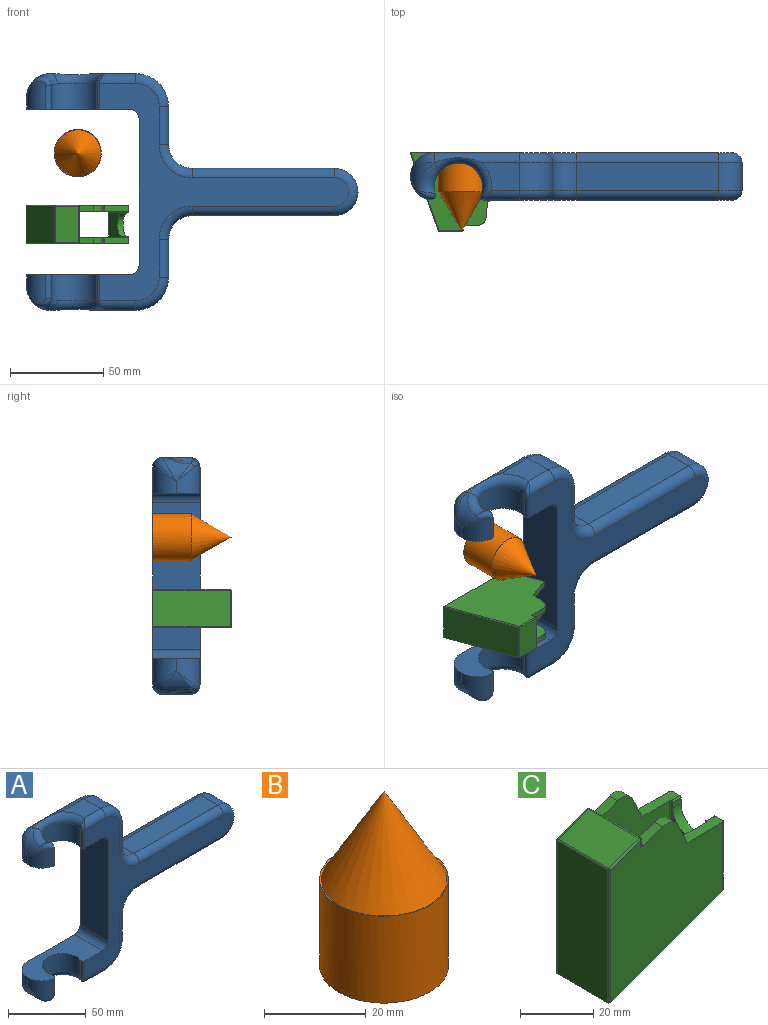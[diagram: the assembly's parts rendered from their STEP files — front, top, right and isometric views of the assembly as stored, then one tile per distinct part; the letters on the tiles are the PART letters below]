
ASSEMBLY  parts=3 mates=2
PART A: 69 faces, bbox 178.8x31.9x135.7 mm
  f0: plane 0.95x0.92mm, normal (0,0,-1), area 0.4mm2, adj f1,f67,f68
  f1: cylinder r=12.7mm len=15.32mm, axis (0,-1,0), area 116.5mm2, adj f0,f2,f64,f65,f66
  f2: bspline ~15x12.7mm, area 107.5mm2, adj f1,f3,f68
  f3: cylinder r=12.7mm len=13.97mm, axis (0,0,-1), area 202.7mm2, adj f2,f4,f63,f64
  f4: plane 55.25x25.4mm, normal (0,0,1), area 896.5mm2, adj f3,f5,f57,f58,f59,f60,f62,f63
  f5: cylinder r=5.08mm len=25.4mm, axis (0,-1,0), area 202.7mm2, adj f4,f6,f57,f63
  f6: plane 78.74x25.4mm, normal (-1,0,0), area 2000mm2, adj f5,f7,f57,f63
  f7: cylinder r=5.08mm len=25.4mm, axis (0,1,0), area 202.7mm2, adj f6,f8,f57,f63
  f8: plane 55.25x25.4mm, normal (0,0,-1), area 896.5mm2, adj f7,f9,f52,f53,f54,f55,f56,f57
  f9: cylinder r=1.59mm len=13.97mm, axis (0,0,1), area 43.1mm2, adj f8,f10,f56,f57
  f10: bspline ~6.71x6.3mm, area 11.8mm2, adj f9,f11,f51
  f11: torus R=18.03mm, axis (0,0,-1), area 267.3mm2, adj f10,f12,f43,f49,f50,f56
  f12: plane 20.77x15.24mm, normal (0,0,1), area 249.5mm2, adj f11,f13,f50,f51
  f13: cylinder r=17.78mm len=17.78mm, axis (0,1,0), area 425.6mm2, adj f12,f14,f41,f42
  f14: torus R=12.7mm, axis (0,-1,0), area 199.7mm2, adj f13,f15,f51,f57
  f15: cylinder r=5.08mm len=20.32mm, axis (0,0,1), area 162.1mm2, adj f14,f16,f42,f57
  f16: torus R=17.78mm, axis (0,-1,0), area 182.3mm2, adj f15,f17,f40,f57
  f17: cylinder r=12.7mm len=15.24mm, axis (0,1,0), area 304mm2, adj f16,f18,f38,f42
  f18: plane 76.2x15.24mm, normal (0,0,1), area 1161.3mm2, adj f17,f19,f37,f40
  f19: cylinder r=5.08mm len=76.2mm, axis (1,0,0), area 608mm2, adj f18,f20,f38,f63
  f20: torus R=7.62mm, axis (0,-1,0), area 272.1mm2, adj f19,f21,f37,f63
  f21: cylinder r=5.08mm len=76.2mm, axis (-1,0,0), area 608mm2, adj f20,f22,f36,f63
  f22: plane 76.2x15.24mm, normal (0,0,-1), area 1161.3mm2, adj f21,f23,f35,f37
  f23: cylinder r=5.08mm len=76.2mm, axis (1,0,0), area 608mm2, adj f22,f24,f25,f57
  f24: torus R=7.62mm, axis (0,-1,0), area 272.1mm2, adj f23,f37,f40,f57
  f25: torus R=17.78mm, axis (0,-1,0), area 182.3mm2, adj f23,f26,f35,f57
  f26: cylinder r=5.08mm len=20.32mm, axis (0,0,1), area 162.1mm2, adj f25,f27,f34,f57
  f27: plane 20.32x15.24mm, normal (1,0,0), area 309.7mm2, adj f26,f28,f30,f35
  f28: cylinder r=5.08mm len=20.32mm, axis (0,0,-1), area 162.1mm2, adj f27,f29,f36,f63
  f29: torus R=12.7mm, axis (0,-1,0), area 199.7mm2, adj f28,f30,f63,f68
  f30: cylinder r=17.78mm len=17.78mm, axis (0,1,0), area 425.6mm2, adj f27,f29,f31,f34
  f31: plane 20.77x15.24mm, normal (0,0,-1), area 249.5mm2, adj f30,f32,f67,f68
  f32: cylinder r=5.08mm len=19.21mm, axis (-1,0,0), area 135.8mm2, adj f31,f33,f34,f57
  f33: bspline ~6.71x6.3mm, area 11.7mm2, adj f32,f58,f67
  f34: torus R=12.7mm, axis (0,-1,0), area 199.7mm2, adj f26,f30,f32,f57
  f35: cylinder r=12.7mm len=15.24mm, axis (0,1,0), area 304mm2, adj f22,f25,f27,f36
  f36: torus R=17.78mm, axis (0,-1,0), area 182.3mm2, adj f21,f28,f35,f63
  f37: cylinder r=12.7mm len=25.4mm, axis (0,-1,0), area 608mm2, adj f18,f20,f22,f24
  f38: torus R=17.78mm, axis (0,-1,0), area 182.3mm2, adj f17,f19,f39,f63
  f39: cylinder r=5.08mm len=20.32mm, axis (0,0,-1), area 162.1mm2, adj f38,f41,f42,f63
  f40: cylinder r=5.08mm len=76.2mm, axis (-1,0,0), area 608mm2, adj f16,f18,f24,f57
  f41: torus R=12.7mm, axis (0,-1,0), area 199.7mm2, adj f13,f39,f50,f63
  f42: plane 20.32x15.24mm, normal (1,0,0), area 309.7mm2, adj f13,f15,f17,f39
  f43: bspline ~20.18x13.12mm, area 151.9mm2, adj f11,f44,f46,f56
  f44: bspline ~11.04x6.91mm, area 51.1mm2, adj f43,f45,f54,f55
  f45: bspline ~10.21x10.21mm, area 13.2mm2, adj f44,f46,f54
  f46: cylinder r=12.7mm len=15.32mm, axis (0,1,0), area 116.5mm2, adj f43,f45,f47,f48,f49,f53
  f47: bspline ~13.31x8.06mm, area 42.8mm2, adj f46,f50,f52
  f48: bspline ~9.27x9.27mm, area 10.4mm2, adj f46,f52
  f49: plane 0.95x0.92mm, normal (0,0,1), area 0.4mm2, adj f11,f46,f50
  f50: cylinder r=5.08mm len=45.72mm, axis (-1,0,0), area 327.3mm2, adj f11,f12,f41,f47,f49,f63
  f51: cylinder r=5.08mm len=19.21mm, axis (1,0,0), area 135.8mm2, adj f10,f12,f14,f57
  f52: cylinder r=12.7mm len=13.97mm, axis (0,0,-1), area 202.7mm2, adj f8,f47,f48,f53,f63
  f53: plane 6.35x0.01mm, normal (-1,0,0), area 0.1mm2, adj f8,f46,f52,f54
  f54: cylinder r=12.7mm len=14.04mm, axis (0,0,-1), area 198.4mm2, adj f8,f44,f45,f53,f55
  f55: cylinder r=2.54mm len=12.55mm, axis (0,0,1), area 65mm2, adj f8,f44,f54,f56
  f56: cylinder r=12.95mm len=25.91mm, axis (0,0,1), area 675mm2, adj f8,f9,f11,f43,f55
  f57: plane 133.51x116.84mm, normal (0,-1,0), area 3452.3mm2, adj f4,f5,f6,f7,f8,f9,f14,f15
  f58: cylinder r=1.59mm len=13.97mm, axis (0,0,1), area 43.1mm2, adj f4,f33,f57,f59
  f59: cylinder r=12.95mm len=25.91mm, axis (0,0,1), area 675mm2, adj f4,f58,f60,f66,f67
  f60: cylinder r=2.54mm len=12.55mm, axis (0,0,-1), area 65mm2, adj f4,f59,f61,f62
  f61: bspline ~11.04x6.91mm, area 51.1mm2, adj f60,f62,f65,f66
  f62: cylinder r=12.7mm len=14.04mm, axis (0,0,-1), area 198.4mm2, adj f4,f60,f61,f64,f65
  f63: plane 160.02x116.84mm, normal (0,1,0), area 4192.9mm2, adj f3,f4,f5,f6,f7,f8,f19,f20
  f64: plane 6.35x0.01mm, normal (-1,0,0), area 0.1mm2, adj f1,f3,f4,f62
  f65: bspline ~10.21x10.21mm, area 13.2mm2, adj f1,f61,f62
  f66: bspline ~19.02x13.12mm, area 151.9mm2, adj f1,f59,f61,f67
  f67: torus R=18.03mm, axis (0,0,-1), area 267.3mm2, adj f0,f31,f33,f59,f66,f68
  f68: cylinder r=5.08mm len=45.72mm, axis (1,0,0), area 327.3mm2, adj f0,f2,f29,f31,f63,f67
PART B: 4 faces, bbox 25.4x25.4x42.2 mm
  f0: plane 25.4x25.4mm, normal (0,0,-1), area 506.7mm2, adj f1
  f1: cylinder r=12.7mm len=25.4mm, axis (0,0,1), area 1672.1mm2, adj f0,f2
  f2: cone r=12.7mm half-angle=60deg, axis (0,0,1), area 30mm2, adj f1,f3
  f3: cone r=12.37mm half-angle=30deg, axis (0,0,-1), area 961.4mm2, adj f2
PART C: 63 faces, bbox 44.7x21.9x49.5 mm
  f0: plane 6.35x6.35mm, normal (0.34,0,-0.94), area 42.9mm2, adj f1,f7,f8,f9
  f1: plane 10.72x6.35mm, normal (1,0,0), area 68.1mm2, adj f0,f7,f9,f10
  f2: sphere r=0.5mm, area 0.3mm2, adj f6,f12,f13
  f3: sphere r=0.5mm, area 0.3mm2, adj f6,f19,f20
  f4: plane 19.64x11.7mm, normal (-0.34,0,0.94), area 244.5mm2, adj f6,f13,f19,f28
  f5: cylinder r=0.5mm len=2.68mm, axis (0,-1,0), area 2.6mm2, adj f21,f22,f31,f40
  f6: cylinder r=0.5mm len=19.64mm, axis (0,-1,0), area 18.9mm2, adj f2,f3,f4,f40
  f7: plane 14.51x7.39mm, normal (0,1,0), area 75.3mm2, adj f0,f1,f8,f10,f42
  f8: plane 11.83x6.35mm, normal (-1,0,0), area 75.1mm2, adj f0,f7,f9,f42
  f9: plane 14.51x7.39mm, normal (0,-1,0), area 75.3mm2, adj f0,f1,f8,f10,f42
  f10: cylinder r=1.57mm len=6.35mm, axis (0,1,0), area 12.2mm2, adj f1,f7,f9,f42
  f11: bspline ~1.19x1.01mm, area 0.6mm2, adj f12,f38,f39,f44
  f12: cylinder r=0.5mm len=2.31mm, axis (0,0,-1), area 1.7mm2, adj f2,f11,f40,f44
  f13: cylinder r=0.5mm len=11.87mm, axis (0.94,0,0.34), area 9.8mm2, adj f2,f4,f29,f44
  f14: cylinder r=0.5mm len=3.22mm, axis (1,0,0), area 2.5mm2, adj f15,f26,f32,f33,f46
  f15: plane 3.18x1.88mm, normal (0,-1,0), area 6mm2, adj f14,f16,f33,f46
  f16: cylinder r=6.35mm len=12.7mm, axis (-1,0,0), area 63.3mm2, adj f15,f17,f33,f46
  f17: plane 3.18x1.88mm, normal (0,1,0), area 6mm2, adj f16,f18,f33,f46
  f18: cylinder r=0.5mm len=3.22mm, axis (-1,0,0), area 2.5mm2, adj f17,f33,f34,f41,f46
  f19: cylinder r=0.5mm len=11.87mm, axis (-0.94,0,-0.34), area 9.8mm2, adj f3,f4,f27,f48
  f20: cylinder r=0.5mm len=2.31mm, axis (0,0,1), area 1.7mm2, adj f3,f21,f40,f48
  f21: bspline ~1.19x1.01mm, area 0.6mm2, adj f5,f20,f22,f48
  f22: plane 7.42x3.19mm, normal (-0.34,0,0.94), area 24.6mm2, adj f5,f21,f23,f31,f48
  f23: cylinder r=4.76mm len=5.94mm, axis (0,1,0), area 22.4mm2, adj f22,f24,f31,f48
  f24: plane 7.32x3.45mm, normal (0.9,0,0.43), area 25.7mm2, adj f23,f25,f31,f48
  f25: cylinder r=0.5mm len=3.18mm, axis (0,1,0), area 1.8mm2, adj f24,f26,f31,f48
  f26: plane 13.97x3.47mm, normal (0,0,1), area 45.3mm2, adj f14,f25,f31,f32,f46,f47,f48
  f27: sphere r=0.5mm, area 0.2mm2, adj f19,f28,f49
  f28: cylinder r=0.5mm len=19.64mm, axis (0,-1,0), area 12mm2, adj f4,f27,f29,f50
  f29: sphere r=0.5mm, area 0.2mm2, adj f13,f28,f51
  f30: cylinder r=0.5mm len=40.86mm, axis (0,0,-1), area 31.8mm2, adj f31,f42,f43,f52
  f31: plane 46.85x37.1mm, normal (0,-1,0), area 1291.2mm2, adj f5,f22,f23,f24,f25,f26,f30,f32
  f32: cylinder r=0.5mm len=22.94mm, axis (0,0,-1), area 17.7mm2, adj f14,f26,f31,f33,f54
  f33: plane 22.35x13.29mm, normal (-1,0,0), area 203.8mm2, adj f14,f15,f16,f17,f18,f32,f41,f55
  f34: plane 13.97x3.47mm, normal (0,0,1), area 45.3mm2, adj f18,f35,f41,f44,f45,f46,f56
  f35: cylinder r=0.5mm len=3.18mm, axis (0,1,0), area 1.8mm2, adj f34,f36,f44,f56
  f36: plane 7.32x3.45mm, normal (0.9,0,0.43), area 25.7mm2, adj f35,f37,f44,f56
  f37: cylinder r=4.76mm len=5.94mm, axis (0,1,0), area 22.4mm2, adj f36,f38,f44,f56
  f38: plane 7.42x3.19mm, normal (-0.34,0,0.94), area 24.6mm2, adj f11,f37,f39,f44,f56
  f39: cylinder r=0.5mm len=2.68mm, axis (0,-1,0), area 2.6mm2, adj f11,f38,f40,f56
  f40: plane 19.64x2.66mm, normal (1,0,0), area 48.5mm2, adj f5,f6,f12,f20,f31,f39,f42,f56
  f41: cylinder r=0.5mm len=22.94mm, axis (0,0,1), area 17.7mm2, adj f18,f33,f34,f56,f57
  f42: plane 14.39x9.62mm, normal (0.34,0,-0.94), area 94.8mm2, adj f7,f8,f9,f10,f30,f31,f40,f43
  f43: plane 40.68x13.29mm, normal (1,0,0), area 540.5mm2, adj f30,f42,f58,f59
  f44: plane 49.3x43.68mm, normal (0,-1,0), area 1569.8mm2, adj f11,f12,f13,f34,f35,f36,f37,f38
  f45: cylinder r=0.5mm len=22.85mm, axis (0,0,1), area 17.9mm2, adj f34,f44,f46,f60
  f46: plane 22.66x19.64mm, normal (1,0,0), area 351.4mm2, adj f14,f15,f16,f17,f18,f26,f34,f45
  f47: cylinder r=0.5mm len=22.85mm, axis (0,0,-1), area 17.9mm2, adj f26,f46,f48,f60
  f48: plane 49.3x43.68mm, normal (0,1,0), area 1569.8mm2, adj f19,f20,f21,f22,f23,f24,f25,f26
  f49: cylinder r=0.5mm len=44.41mm, axis (0,0,-1), area 34.8mm2, adj f27,f48,f50,f60
  f50: plane 44.41x19.64mm, normal (-1,0,0), area 872.1mm2, adj f28,f49,f51,f60
  f51: cylinder r=0.5mm len=44.41mm, axis (0,0,1), area 34.8mm2, adj f29,f44,f50,f60
  f52: bspline ~1.54x1.52mm, area 2.1mm2, adj f30,f53,f59,f60
  f53: cylinder r=1mm len=37.44mm, axis (0.94,0,0.34), area 62mm2, adj f31,f52,f54,f60
  f54: bspline ~1.87x1.54mm, area 2.4mm2, adj f32,f53,f55,f60
  f55: cylinder r=1mm len=13.29mm, axis (0,-1,0), area 25.5mm2, adj f33,f54,f57,f60
  f56: plane 46.85x37.1mm, normal (0,1,0), area 1291.2mm2, adj f34,f35,f36,f37,f38,f39,f40,f41
  f57: bspline ~1.87x1.52mm, area 2.4mm2, adj f41,f55,f60,f61
  f58: cylinder r=0.5mm len=40.86mm, axis (0,0,-1), area 31.8mm2, adj f42,f43,f56,f62
  f59: cylinder r=1mm len=13.29mm, axis (0,1,0), area 16.2mm2, adj f43,f52,f60,f62
  f60: plane 44.55x20.74mm, normal (0.34,0,-0.94), area 283.2mm2, adj f44,f45,f46,f47,f48,f49,f50,f51
  f61: cylinder r=1mm len=37.44mm, axis (-0.94,0,-0.34), area 62mm2, adj f56,f57,f60,f62
  f62: bspline ~1.54x1.54mm, area 2.1mm2, adj f58,f59,f60,f61
PLACE A t=(-14.91,-2.14,31.51)mm
PLACE B rot(axis=(1,0,0),90deg) t=(-13.13,-52.94,58.18)mm
PLACE C rot(axis=(0.97,0.17,0.17),91.7deg) t=(-72.26,-12.06,13.98)mm
MATE planar C.f60 <-> A.f63  axis (0,1,0) through (-81.38,10.56,13.98)mm
MATE planar B.f1 <-> A.f63  axis (0,1,0) through (-76.38,10.56,52.34)mm
